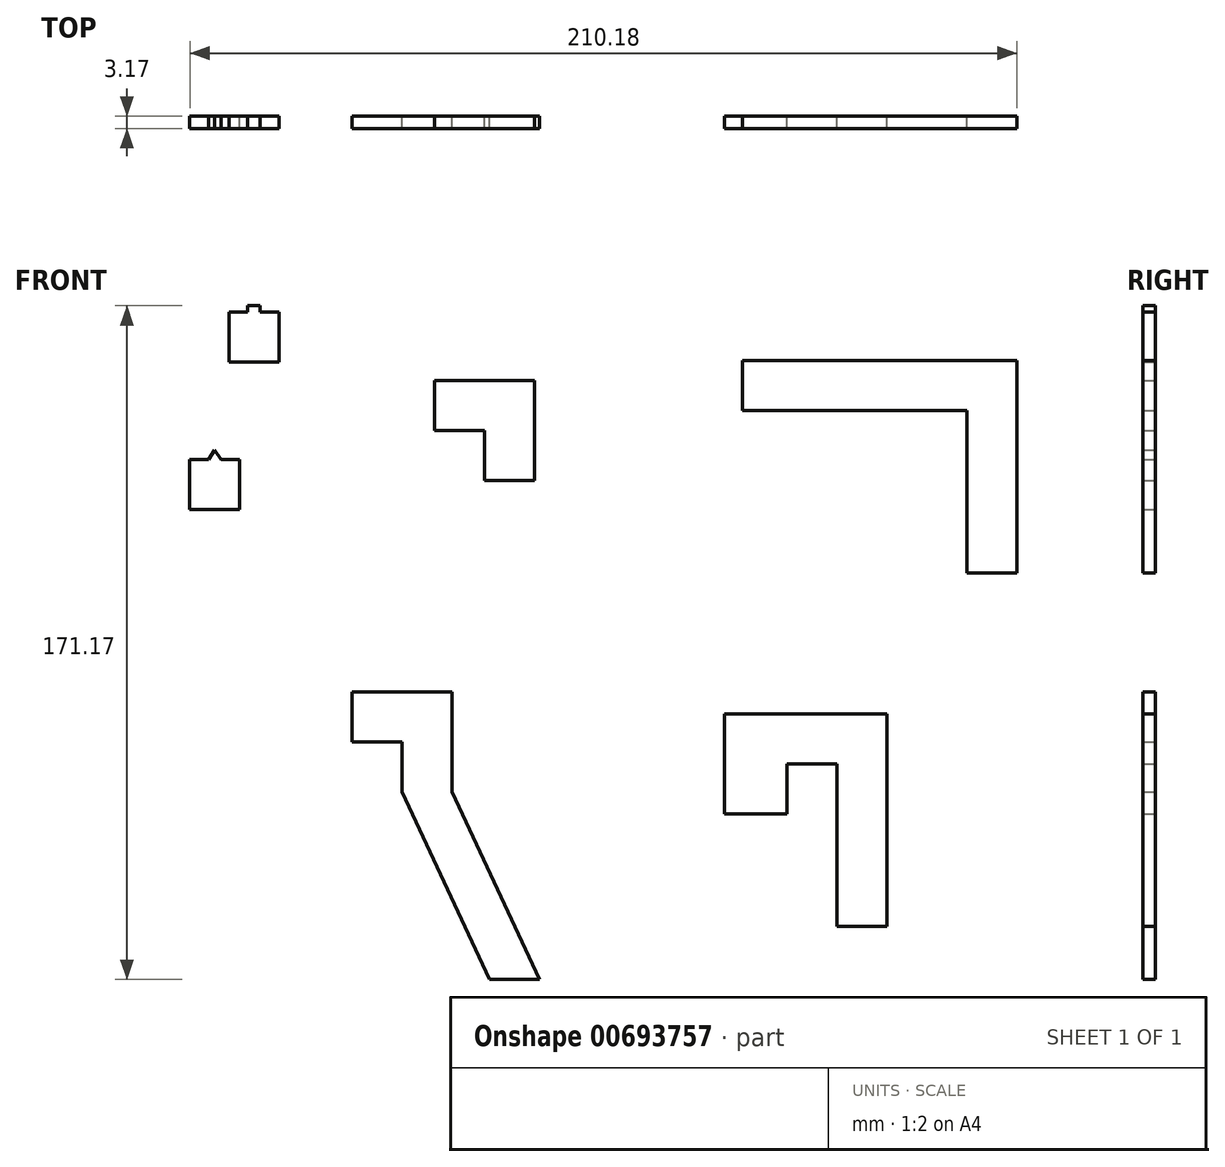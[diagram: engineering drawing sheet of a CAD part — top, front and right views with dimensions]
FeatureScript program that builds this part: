
annotation { "Feature Type Name" : "Feature", "Feature Type Description" : "" }
export const myFeature = defineFeature(function(context is Context, id is Id, definition is map)
    precondition{}
    {
        {
            var Q0;
            Q0=qCreatedBy(makeId("Front.planeOp"),FACE);
            var sketch = newSketch(context, id + "F0", { "sketchPlane" : qUnion([Q0])});
            skLineSegment(sketch, "E0", {"start": v(-41.88, 26.54) * mm, "end": v(-16.48, 26.54) * mm});
            skLineSegment(sketch, "E1", {"start": v(-16.48, 26.54) * mm, "end": v(-16.48, 1.14) * mm});
            skLineSegment(sketch, "E2", {"start": v(-41.88, 26.54) * mm, "end": v(-41.88, 13.84) * mm});
            skLineSegment(sketch, "E3", {"start": v(-41.88, 13.84) * mm, "end": v(-29.18, 13.84) * mm});
            skLineSegment(sketch, "E4", {"start": v(-29.18, 13.84) * mm, "end": v(-29.18, 1.14) * mm});
            skLineSegment(sketch, "E5", {"start": v(-6.95, -46.48) * mm, "end": v(-29.18, 1.14) * mm});
            skLineSegment(sketch, "E6", {"start": v(5.75, -46.48) * mm, "end": v(-16.48, 1.14) * mm});
            skPoint(sketch, "E7.end.orphan", {"position": v(-41.88, 1.14) * mm});
            skLineSegment(sketch, "E8", {"start": v(-6.95, -46.48) * mm, "end": v(5.75, -46.48) * mm});
            skLineSegment(sketch, "E9", {"start": v(-20.95, 105.62) * mm, "end": v(4.45, 105.62) * mm});
            skLineSegment(sketch, "E10", {"start": v(4.45, 105.62) * mm, "end": v(4.45, 80.22) * mm});
            skLineSegment(sketch, "E11", {"start": v(4.45, 80.22) * mm, "end": v(-8.25, 80.22) * mm});
            skLineSegment(sketch, "E12", {"start": v(-8.25, 80.22) * mm, "end": v(-8.25, 92.92) * mm});
            skLineSegment(sketch, "E13", {"start": v(-8.25, 92.92) * mm, "end": v(-20.95, 92.92) * mm});
            skLineSegment(sketch, "E14", {"start": v(-20.95, 92.92) * mm, "end": v(-20.95, 105.62) * mm});
            skLineSegment(sketch, "E15", {"start": v(81.29, -33.04) * mm, "end": v(93.99, -33.04) * mm});
            skLineSegment(sketch, "E16", {"start": v(93.99, -33.04) * mm, "end": v(93.99, 20.93) * mm});
            skLineSegment(sketch, "E17", {"start": v(93.99, 20.93) * mm, "end": v(52.71, 20.93) * mm});
            skLineSegment(sketch, "E18", {"start": v(52.71, 20.93) * mm, "end": v(52.71, -4.47) * mm});
            skLineSegment(sketch, "E19", {"start": v(52.71, -4.47) * mm, "end": v(68.59, -4.47) * mm});
            skLineSegment(sketch, "E20", {"start": v(68.59, -4.47) * mm, "end": v(68.59, 8.23) * mm});
            skLineSegment(sketch, "E21", {"start": v(68.59, 8.23) * mm, "end": v(81.29, 8.23) * mm});
            skLineSegment(sketch, "E22", {"start": v(81.29, 8.23) * mm, "end": v(81.29, -33.04) * mm});
            skLineSegment(sketch, "E23", {"start": v(57.25, 110.8) * mm, "end": v(127.1, 110.8) * mm});
            skLineSegment(sketch, "E24", {"start": v(127.1, 110.8) * mm, "end": v(127.1, 56.83) * mm});
            skLineSegment(sketch, "E25", {"start": v(127.1, 56.83) * mm, "end": v(114.4, 56.83) * mm});
            skLineSegment(sketch, "E26", {"start": v(57.25, 110.8) * mm, "end": v(57.25, 98.1) * mm});
            skLineSegment(sketch, "E27", {"start": v(57.25, 98.1) * mm, "end": v(114.4, 98.1) * mm});
            skLineSegment(sketch, "E28", {"start": v(114.4, 98.1) * mm, "end": v(114.4, 56.83) * mm});
            skLineSegment(sketch, "E29.bottom", {"start": v(-73.14, 123.1) * mm, "end": v(-68.38, 123.1) * mm});
            skLineSegment(sketch, "E29.top", {"start": v(-73.14, 110.4) * mm, "end": v(-60.44, 110.4) * mm});
            skLineSegment(sketch, "E29.left", {"start": v(-73.14, 123.1) * mm, "end": v(-73.14, 110.4) * mm});
            skLineSegment(sketch, "E29.right", {"start": v(-60.44, 123.1) * mm, "end": v(-60.44, 110.4) * mm});
            skLineSegment(sketch, "E30.bottom", {"start": v(-68.38, 124.69) * mm, "end": v(-65.2, 124.69) * mm});
            skLineSegment(sketch, "E30.left", {"start": v(-68.38, 124.69) * mm, "end": v(-68.38, 123.1) * mm});
            skLineSegment(sketch, "E30.right", {"start": v(-65.2, 124.69) * mm, "end": v(-65.2, 123.1) * mm});
            skPoint(sketch, "E30.middle", {"position": v(-66.8, 123.1) * mm});
            skPoint(sketch, "E30.top.start.orphan", {"position": v(-68.38, 121.51) * mm});
            skPoint(sketch, "E31.orphan", {"position": v(-65.2, 121.51) * mm});
            skLineSegment(sketch, "E32.trimOffspring", {"start": v(-65.2, 123.1) * mm, "end": v(-60.44, 123.1) * mm});
            skLineSegment(sketch, "E33.bottom", {"start": v(-83.08, 85.61) * mm, "end": v(-78.32, 85.61) * mm});
            skLineSegment(sketch, "E33.top", {"start": v(-83.08, 72.91) * mm, "end": v(-70.38, 72.91) * mm});
            skLineSegment(sketch, "E33.left", {"start": v(-83.08, 85.61) * mm, "end": v(-83.08, 72.91) * mm});
            skLineSegment(sketch, "E33.right", {"start": v(-70.38, 85.61) * mm, "end": v(-70.38, 72.91) * mm});
            skPoint(sketch, "E34.middle", {"position": v(-76.73, 85.61) * mm});
            skPoint(sketch, "E34.top.start.orphan", {"position": v(-78.32, 84.03) * mm});
            skPoint(sketch, "E35.orphan", {"position": v(-75.15, 84.03) * mm});
            skLineSegment(sketch, "E36.trimOffspring", {"start": v(-75.15, 85.61) * mm, "end": v(-70.38, 85.61) * mm});
            skLineSegment(sketch, "E37", {"start": v(-76.73, 88.01) * mm, "end": v(-78.32, 85.61) * mm});
            skLineSegment(sketch, "E38", {"start": v(-76.73, 88.01) * mm, "end": v(-75.15, 85.61) * mm});
            skPoint(sketch, "E34.right.start.orphan", {"position": v(-75.15, 87.2) * mm});
            skPoint(sketch, "E39.start.orphan", {"position": v(-76.73, 87.2) * mm});
            skPoint(sketch, "E34.left.start.orphan", {"position": v(-78.32, 87.2) * mm});
            skSolve(sketch);
        }
        {
            var Q0;
            Q0 = qSketchRegion(id + "F0", true);
            extrude(context, id + "F1", {"entities" : qUnion([Q0]), "depth" : 3.17 * mm, "offsetDistance" : 25.4 * mm});
        }
    });
